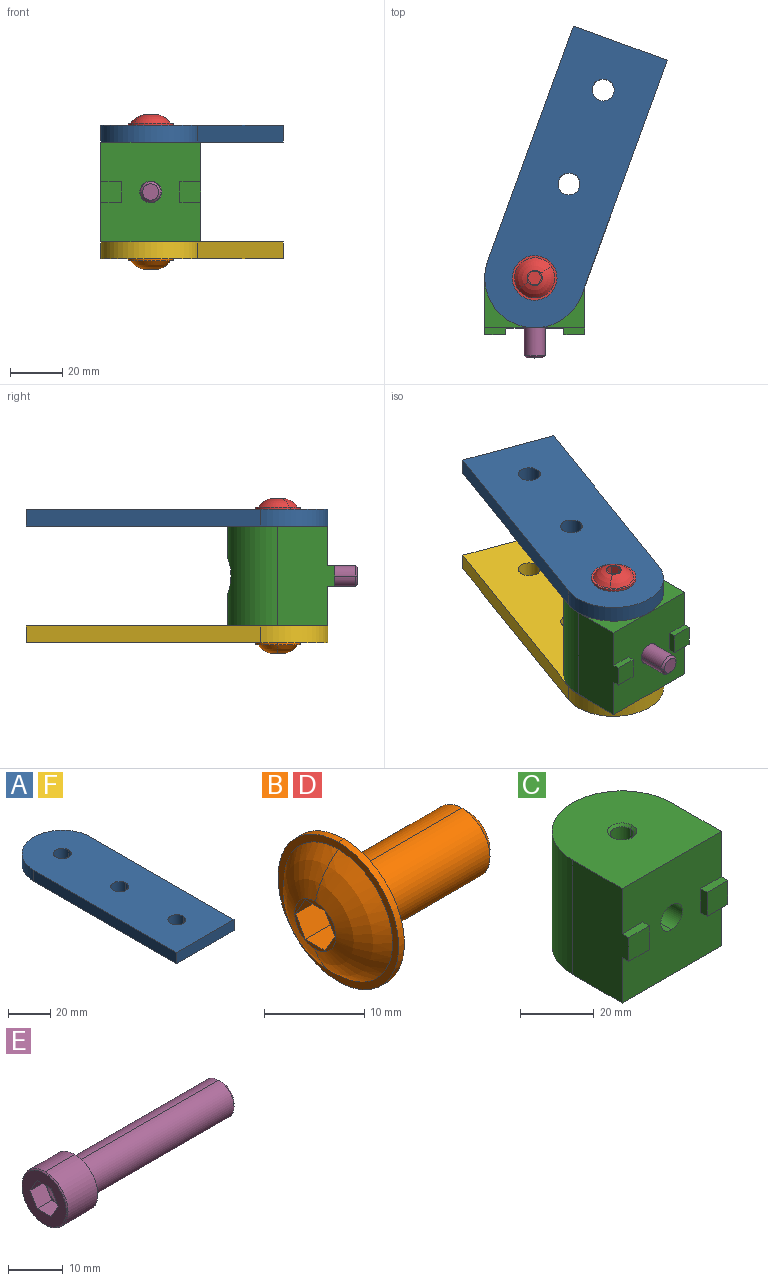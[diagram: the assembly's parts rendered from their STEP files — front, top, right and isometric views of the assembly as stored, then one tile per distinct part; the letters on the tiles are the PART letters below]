
ASSEMBLY  parts=6 mates=12
PART A: 12 faces, bbox 38.1x114.3x6.4 mm
  f0: cylinder r=19.05mm len=38.1mm, axis (0,0,1), area 380mm2, adj f1,f3,f4,f7
  f1: plane 95.25x6.35mm, normal (1,0,0), area 604.8mm2, adj f0,f2,f4,f7
  f2: plane 38.1x6.35mm, normal (0,-1,0), area 241.9mm2, adj f1,f3,f4,f7
  f3: plane 95.25x6.35mm, normal (-1,0,0), area 604.8mm2, adj f0,f2,f4,f7
  f4: plane 114.3x38.1mm, normal (0,0,1), area 4035.5mm2, adj f0,f1,f2,f3,f5,f6,f8,f9
  f5: cylinder r=4.17mm len=8.33mm, axis (0,0,1), area 83.1mm2, adj f4,f6,f7
  f6: cylinder r=4.17mm len=8.33mm, axis (0,0,1), area 83.1mm2, adj f4,f5,f7
  f7: plane 114.3x38.1mm, normal (0,0,-1), area 4035.5mm2, adj f0,f1,f2,f3,f5,f6,f8,f9
  f8: cylinder r=4.17mm len=8.33mm, axis (0,0,1), area 83.1mm2, adj f4,f7,f9
  f9: cylinder r=4.17mm len=8.33mm, axis (0,0,1), area 83.1mm2, adj f4,f7,f8
  f10: cylinder r=4.17mm len=8.33mm, axis (0,0,1), area 83.1mm2, adj f4,f7,f11
  f11: cylinder r=4.17mm len=8.33mm, axis (0,0,1), area 83.1mm2, adj f4,f7,f10
PART B: 19 faces, bbox 21.5x17x17 mm
  f0: torus R=0.76mm, axis (1,0,0), area 101mm2, adj f1,f2,f10
  f1: torus R=0.76mm, axis (1,0,0), area 101mm2, adj f0,f2,f10
  f2: plane 5.79x5.79mm, normal (-1,0,0), area 6.2mm2, adj f0,f1,f3,f4,f5,f6,f7,f8
  f3: plane 3.56x2.41mm, normal (0,-0.87,-0.5), area 9.9mm2, adj f2,f4,f8,f9
  f4: plane 3.56x2.79mm, normal (0,0,-1), area 9.9mm2, adj f2,f3,f5,f9
  f5: plane 3.56x2.41mm, normal (0,0.87,-0.5), area 9.9mm2, adj f2,f4,f6,f9
  f6: plane 3.56x2.41mm, normal (0,0.87,0.5), area 9.9mm2, adj f2,f5,f7,f9
  f7: plane 3.56x2.79mm, normal (0,0,1), area 9.9mm2, adj f2,f6,f8,f9
  f8: plane 3.56x2.41mm, normal (0,-0.87,0.5), area 9.9mm2, adj f2,f3,f7,f9
  f9: plane 5.57x4.83mm, normal (-1,0,0), area 20.2mm2, adj f3,f4,f5,f6,f7,f8
  f10: plane 17.02x17.02mm, normal (-1,0,0), area 43.2mm2, adj f0,f1,f11,f12
  f11: cylinder r=8.51mm len=17.02mm, axis (-1,0,0), area 21.7mm2, adj f10,f12,f13
  f12: cylinder r=8.51mm len=17.02mm, axis (-1,0,0), area 21.7mm2, adj f10,f11,f13
  f13: plane 17.02x17.02mm, normal (1,0,0), area 178mm2, adj f11,f12,f14,f15
  f14: cylinder r=3.97mm len=16.62mm, axis (-1,0,0), area 207.3mm2, adj f13,f15,f17
  f15: cylinder r=3.97mm len=16.62mm, axis (-1,0,0), area 207.3mm2, adj f13,f14,f16
  f16: cone r=3.97mm half-angle=45deg, axis (-1,0,0), area 13.2mm2, adj f15,f17,f18
  f17: cone r=3.97mm half-angle=45deg, axis (-1,0,0), area 13.2mm2, adj f14,f16,f18
  f18: plane 6.26x6.26mm, normal (1,0,0), area 30.8mm2, adj f16,f17
PART C: 27 faces, bbox 38.1x40.6x38.1 mm
  f0: cylinder r=4.17mm len=26.67mm, axis (0,1,0), area 313.6mm2, adj f1,f2,f3,f11,f17,f21,f22
  f1: cylinder r=4.17mm len=26.67mm, axis (0,1,0), area 313.6mm2, adj f0,f2,f3,f11,f17,f21,f22
  f2: cylinder r=3.21mm len=15.63mm, axis (0,0,1), area 149.8mm2, adj f0,f1,f3,f5
  f3: cylinder r=3.21mm len=15.63mm, axis (0,0,1), area 149.8mm2, adj f0,f1,f2,f4
  f4: cone r=3.21mm half-angle=45deg, axis (0,0,-1), area 12.2mm2, adj f3,f5,f6
  f5: cone r=3.21mm half-angle=45deg, axis (0,0,-1), area 12.2mm2, adj f2,f4,f6
  f6: plane 38.1x38.1mm, normal (0,0,-1), area 1246.4mm2, adj f4,f5,f7,f11,f13,f14
  f7: plane 38.1x21.59mm, normal (1,0,0), area 745.9mm2, adj f6,f8,f9,f11,f12,f14,f18
  f8: plane 7.92x2.54mm, normal (0,0,-1), area 20.1mm2, adj f7,f9,f10,f11
  f9: plane 7.93x7.92mm, normal (0,-1,0), area 62.8mm2, adj f7,f8,f10,f12
  f10: plane 7.93x2.54mm, normal (-1,0,0), area 20.1mm2, adj f8,f9,f11,f12
  f11: plane 38.1x38.1mm, normal (0,-1,0), area 1271.5mm2, adj f0,f1,f6,f7,f8,f10,f12,f13
  f12: plane 7.92x2.54mm, normal (0,0,1), area 20.1mm2, adj f7,f9,f10,f11
  f13: plane 38.1x21.59mm, normal (-1,0,0), area 745.9mm2, adj f6,f11,f14,f18,f23,f24,f26
  f14: cylinder r=19.05mm len=38.1mm, axis (0,0,1), area 2143.7mm2, adj f6,f7,f13,f15,f16,f18
  f15: cylinder r=6.54mm len=13.08mm, axis (0,1,0), area 223.1mm2, adj f14,f16,f17
  f16: cylinder r=6.54mm len=13.08mm, axis (0,1,0), area 223.1mm2, adj f14,f15,f17
  f17: plane 13.08x13.08mm, normal (0,1,0), area 79.9mm2, adj f0,f1,f15,f16
  f18: plane 38.1x38.1mm, normal (0,0,1), area 1246.4mm2, adj f7,f11,f13,f14,f19,f20
  f19: cone r=3.97mm half-angle=45deg, axis (0,0,1), area 12.2mm2, adj f18,f20,f22
  f20: cone r=3.97mm half-angle=45deg, axis (0,0,1), area 12.2mm2, adj f18,f19,f21
  f21: cylinder r=3.21mm len=15.63mm, axis (0,0,1), area 149.8mm2, adj f0,f1,f20,f22
  f22: cylinder r=3.21mm len=15.63mm, axis (0,0,1), area 149.8mm2, adj f0,f1,f19,f21
  f23: plane 7.93x2.54mm, normal (0,0,1), area 20.1mm2, adj f11,f13,f24,f25
  f24: plane 7.93x7.93mm, normal (0,-1,0), area 62.8mm2, adj f13,f23,f25,f26
  f25: plane 7.93x2.54mm, normal (1,0,0), area 20.1mm2, adj f11,f23,f24,f26
  f26: plane 7.93x2.54mm, normal (0,0,-1), area 20.1mm2, adj f11,f13,f24,f25
PART D: same geometry as B
PART E: 27 faces, bbox 46x11.9x11.9 mm
  f0: cone r=3.17mm half-angle=60deg, axis (-1,0,0), area 18.3mm2, adj f1,f9,f10,f24
  f1: cone r=3.17mm half-angle=60deg, axis (-1,0,0), area 18.3mm2, adj f0,f2,f25,f26
  f2: plane 2.75x1.59mm, normal (-1,0,0), area 0.5mm2, adj f1,f3,f4
  f3: plane 3.84x3.67mm, normal (0,0,1), area 14.1mm2, adj f2,f4,f8,f9,f11
  f4: plane 3.84x3.18mm, normal (0,-0.87,0.5), area 14.1mm2, adj f2,f3,f5,f11,f26
  f5: plane 3.84x3.18mm, normal (0,-0.87,-0.5), area 14.1mm2, adj f4,f6,f11,f25,f26
  f6: plane 3.84x3.67mm, normal (0,0,-1), area 14.1mm2, adj f5,f7,f11,f24,f25
  f7: plane 3.84x3.18mm, normal (0,0.87,-0.5), area 14.1mm2, adj f6,f8,f10,f11,f24
  f8: plane 3.84x3.18mm, normal (0,0.87,0.5), area 14.1mm2, adj f3,f7,f9,f10,f11
  f9: plane 2.75x1.59mm, normal (-1,0,0), area 0.5mm2, adj f0,f3,f8
  f10: plane 3.18x0.92mm, normal (-1,0,0), area 0.5mm2, adj f0,f7,f8
  f11: plane 11.44x11.44mm, normal (-1,0,0), area 67.8mm2, adj f3,f4,f5,f6,f7,f8,f12,f13
  f12: cone r=5.72mm half-angle=45deg, axis (1,0,0), area 6.2mm2, adj f11,f13,f15
  f13: cone r=5.72mm half-angle=45deg, axis (1,0,0), area 6.2mm2, adj f11,f12,f14
  f14: cylinder r=5.96mm len=11.91mm, axis (-1,0,0), area 143.8mm2, adj f13,f15,f16
  f15: cylinder r=5.96mm len=11.91mm, axis (-1,0,0), area 143.8mm2, adj f12,f14,f16
  f16: plane 11.91x11.91mm, normal (1,0,0), area 55.9mm2, adj f14,f15,f17,f18
  f17: torus R=4.21mm, axis (1,0,0), area 4.8mm2, adj f16,f18,f20
  f18: torus R=4.21mm, axis (1,0,0), area 4.8mm2, adj f16,f17,f19
  f19: cylinder r=3.97mm len=37.02mm, axis (-1,0,0), area 461.6mm2, adj f18,f20,f22
  f20: cylinder r=3.97mm len=37.02mm, axis (-1,0,0), area 461.6mm2, adj f17,f19,f21
  f21: cone r=3.97mm half-angle=45deg, axis (-1,0,0), area 13.2mm2, adj f20,f22,f23
  f22: cone r=3.97mm half-angle=45deg, axis (-1,0,0), area 13.2mm2, adj f19,f21,f23
  f23: plane 6.26x6.26mm, normal (1,0,0), area 30.8mm2, adj f21,f22
  f24: plane 2.75x1.59mm, normal (-1,0,0), area 0.5mm2, adj f0,f6,f7
  f25: plane 2.75x1.59mm, normal (-1,0,0), area 0.5mm2, adj f1,f5,f6
  f26: plane 3.18x0.92mm, normal (-1,0,0), area 0.5mm2, adj f1,f4,f5
PART F: same geometry as A
PLACE A rot(axis=(0,0,1),160deg) t=(32.64,108.53,19.05)mm
PLACE B rot(axis=(0.71,0,0.71),180deg) t=(0,19.05,-25.4)mm
PLACE C at identity fixed
PLACE D rot(axis=(-0.28,0.92,0.28),95deg) t=(0,19.05,25.4)mm
PLACE E rot(axis=(0.58,-0.58,-0.58),120deg) t=(0,26.67,0)mm
PLACE F rot(axis=(0,0,1),160deg) t=(32.64,108.53,-25.4)mm
MATE planar A.f2 <-> F.f2  axis (0.34,0.94,0) through (32.64,108.53,22.22)mm
MATE planar C.f6 <-> F.f4  axis (0,0,-1) through (19.05,9.52,-19.05)mm
MATE cylindrical D.f11 <-> A.f0  axis (0,0,1) through (0,19.05,25.4)mm
MATE planar A.f1 <-> F.f1  axis (-0.94,0.34,0) through (-1.58,70.32,22.22)mm
MATE parallel E.f6 <-> C.f7  axis (1,0,0) through (-3.18,32.68,0)mm
MATE planar B.f0 <-> F.f7  axis (0,0,1) through (0,19.05,-25.4)mm
MATE cylindrical F.f0 <-> C.f2  axis (0,0,1) through (0,19.05,-25.4)mm
MATE cylindrical E.f0 <-> C.f0  axis (0,1,0) through (0,7.92,0)mm
MATE planar D.f13 <-> A.f4  axis (0,0,-1) through (-3.28,16.82,25.4)mm
MATE cylindrical B.f11 <-> F.f0  axis (0,0,-1) through (0,19.05,-25.4)mm
MATE planar A.f7 <-> C.f18  axis (0,0,-1) through (13.76,56.76,19.05)mm
MATE planar E.f0 <-> C.f0  axis (0,-1,0) through (0,26.67,0)mm
